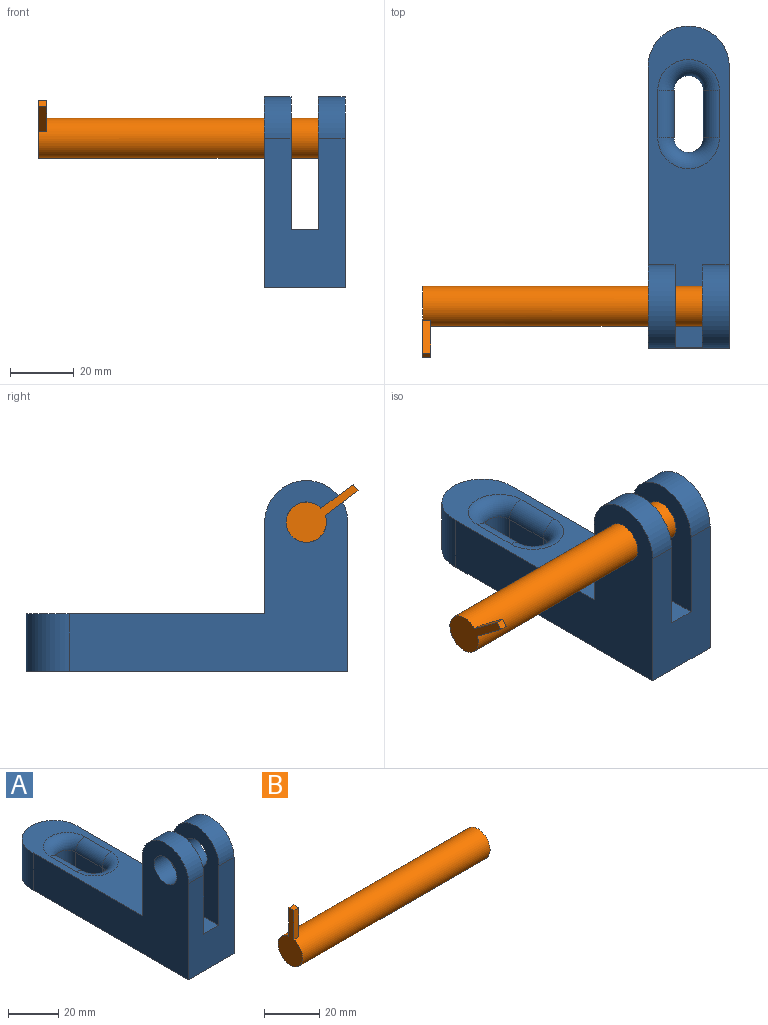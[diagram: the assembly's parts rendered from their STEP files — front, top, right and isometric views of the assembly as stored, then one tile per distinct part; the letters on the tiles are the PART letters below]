
ASSEMBLY  parts=2 mates=1
PART A: 23 faces, bbox 25.5x100.9x59.8 mm
  f0: plane 87.25x59.78mm, normal (1,0,0), area 2461.7mm2, adj f2,f4,f6,f7,f9,f10,f13
  f1: plane 87.25x59.78mm, normal (-1,0,0), area 2461.7mm2, adj f3,f5,f6,f8,f9,f10,f13
  f2: plane 28.72x8.43mm, normal (0,1,0), area 242.2mm2, adj f0,f4,f10,f11
  f3: plane 28.72x8.43mm, normal (0,1,0), area 242.2mm2, adj f1,f5,f10,f12
  f4: cylinder r=13.03mm len=26.05mm, axis (-1,0,0), area 345.1mm2, adj f0,f2,f6,f11
  f5: cylinder r=13.03mm len=26.05mm, axis (-1,0,0), area 345.1mm2, adj f1,f3,f6,f12
  f6: plane 46.76x25.4mm, normal (0,-1,0), area 942.5mm2, adj f0,f1,f4,f5,f9,f10,f11,f12
  f7: cylinder r=6.35mm len=12.7mm, axis (-1,0,0), area 336.5mm2, adj f0,f11
  f8: cylinder r=6.35mm len=12.7mm, axis (-1,0,0), area 336.5mm2, adj f1,f12
  f9: plane 88.17x25.4mm, normal (0,0,-1), area 2037.4mm2, adj f0,f1,f6,f14,f15,f16,f17,f18
  f10: plane 100.91x25.47mm, normal (0,0,1), area 1474.1mm2, adj f0,f1,f2,f3,f6,f11,f12,f13
  f11: plane 41.75x26.05mm, normal (-1,0,0), area 888.1mm2, adj f2,f4,f6,f7,f10
  f12: plane 41.75x26.05mm, normal (1,0,0), area 888.1mm2, adj f3,f5,f6,f8,f10
  f13: cylinder r=12.73mm len=25.47mm, axis (0,0,1), area 754.6mm2, adj f0,f1,f10,f14
  f14: plane 25.47x13.65mm, normal (0,0,-1), area 254.7mm2, adj f9,f13
  f15: cylinder r=4.57mm len=12.96mm, axis (0,0,1), area 186.1mm2, adj f9,f16,f18,f19
  f16: plane 14.92x12.96mm, normal (-1,0,0), area 193.3mm2, adj f9,f15,f17,f20
  f17: cylinder r=4.57mm len=12.96mm, axis (0,0,1), area 186.1mm2, adj f9,f16,f18,f22
  f18: plane 14.92x12.96mm, normal (1,0,0), area 193.3mm2, adj f9,f15,f17,f21
  f19: torus R=9.65mm, axis (0,0,1), area 160.9mm2, adj f10,f15,f20,f21
  f20: cylinder r=5.08mm len=14.92mm, axis (0,-1,0), area 119.1mm2, adj f10,f16,f19,f22
  f21: cylinder r=5.08mm len=14.92mm, axis (0,1,0), area 119.1mm2, adj f10,f18,f19,f22
  f22: torus R=9.65mm, axis (0,0,1), area 160.9mm2, adj f10,f17,f20,f21
PART B: 7 faces, bbox 96x12.6x25.2 mm
  f0: cylinder r=6.3mm len=96.01mm, axis (1,0,0), area 3791.3mm2, adj f1,f2,f3,f5,f6
  f1: plane 25.15x12.59mm, normal (-1,0,0), area 156.5mm2, adj f0,f3,f4,f5
  f2: plane 12.59x12.59mm, normal (1,0,0), area 124.5mm2, adj f0
  f3: plane 12.82x2.54mm, normal (0,-1,0), area 32.6mm2, adj f0,f1,f4,f6
  f4: plane 2.54x2.53mm, normal (0,0,1), area 6.4mm2, adj f1,f3,f5,f6
  f5: plane 12.6x2.54mm, normal (0,1,0), area 32mm2, adj f0,f1,f4,f6
  f6: plane 12.82x2.53mm, normal (1,0,0), area 32mm2, adj f0,f3,f4,f5
PLACE A t=(29.9,-27.35,13.57)mm fixed
PLACE B rot(axis=(1,0,0),53.3deg) t=(-18.11,-10.61,46.56)mm
MATE revolute A.f4 <-> B.f0  axis (1,0,0) through (55.3,-51.81,46.72)mm
